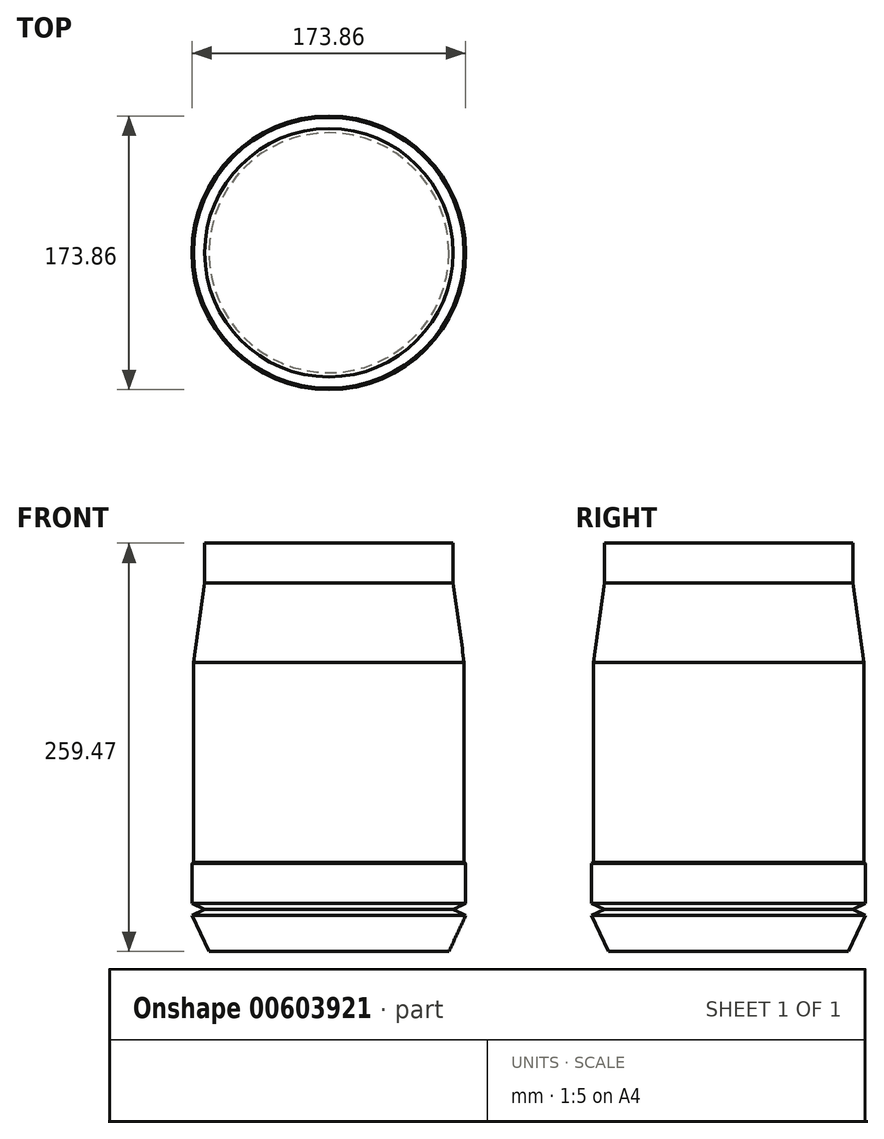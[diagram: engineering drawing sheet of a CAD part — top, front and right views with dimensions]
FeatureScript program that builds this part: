
annotation { "Feature Type Name" : "Feature", "Feature Type Description" : "" }
export const myFeature = defineFeature(function(context is Context, id is Id, definition is map)
    precondition{}
    {
        {
            var Q0;
            Q0=qCreatedBy(makeId("Front.planeOp"),FACE);
            var sketch = newSketch(context, id + "F0", { "sketchPlane" : qUnion([Q0])});
            skLineSegment(sketch, "E0", {"start": v(0, 0) * mm, "end": v(0, -254) * mm});
            skLineSegment(sketch, "E1", {"start": v(0, -254) * mm, "end": v(-76.2, -254) * mm});
            skLineSegment(sketch, "E2", {"start": v(-76.2, -254) * mm, "end": v(-86.93, -230.98) * mm});
            skLineSegment(sketch, "E3", {"start": v(-86.93, -230.98) * mm, "end": v(-78.87, -227.22) * mm});
            skLineSegment(sketch, "E4", {"start": v(-78.87, -227.22) * mm, "end": v(-86.93, -223.42) * mm});
            skLineSegment(sketch, "E5", {"start": v(-86.93, -223.42) * mm, "end": v(-86.93, -198.02) * mm});
            skLineSegment(sketch, "E6", {"start": v(-86.93, -198.02) * mm, "end": v(-85.95, -197.21) * mm});
            skLineSegment(sketch, "E7", {"start": v(-85.95, -197.21) * mm, "end": v(-85.95, -70.21) * mm});
            skLineSegment(sketch, "E8", {"start": v(-85.95, -70.21) * mm, "end": v(-78.87, -19.93) * mm});
            skLineSegment(sketch, "E9", {"start": v(-78.87, -19.93) * mm, "end": v(0, -19.93) * mm});
            skSolve(sketch);
        }
        {
            var Q0;
            {var subQ0=sQuery(id+"F0.wireOp",EDGE,"E1");Q0=makeQuery(id+"F0.imprint","IMPRINT",FACE,{"disambiguationData":[TD([[makeQuery(id+"F0.imprint","IMPRINT",EDGE,{"derivedFrom":subQ0}),-1.0]])]});}
            var Q1;
            Q1=sQuery(id+"F0.wireOp",EDGE,"E0");
            revolve(context, id + "F1", {"entities" : qUnion([Q0]), "axis" : qUnion([Q1]), "revolveType" : RevolveType.FULL});
        }
        {
            var Q0;
            Q0=makeQuery(id+"F1.opRevolve","SWEPT_FACE",FACE,{"disambiguationData":[OSD([sQuery(id+"F0.wireOp",EDGE,"E9")])]});
            extrude(context, id + "F2", {"entities" : qUnion([Q0]), "operationType" : NewBodyOperationType.ADD, "depth" : 25.4 * mm, "offsetDistance" : 25.4 * mm});
        }
    });
